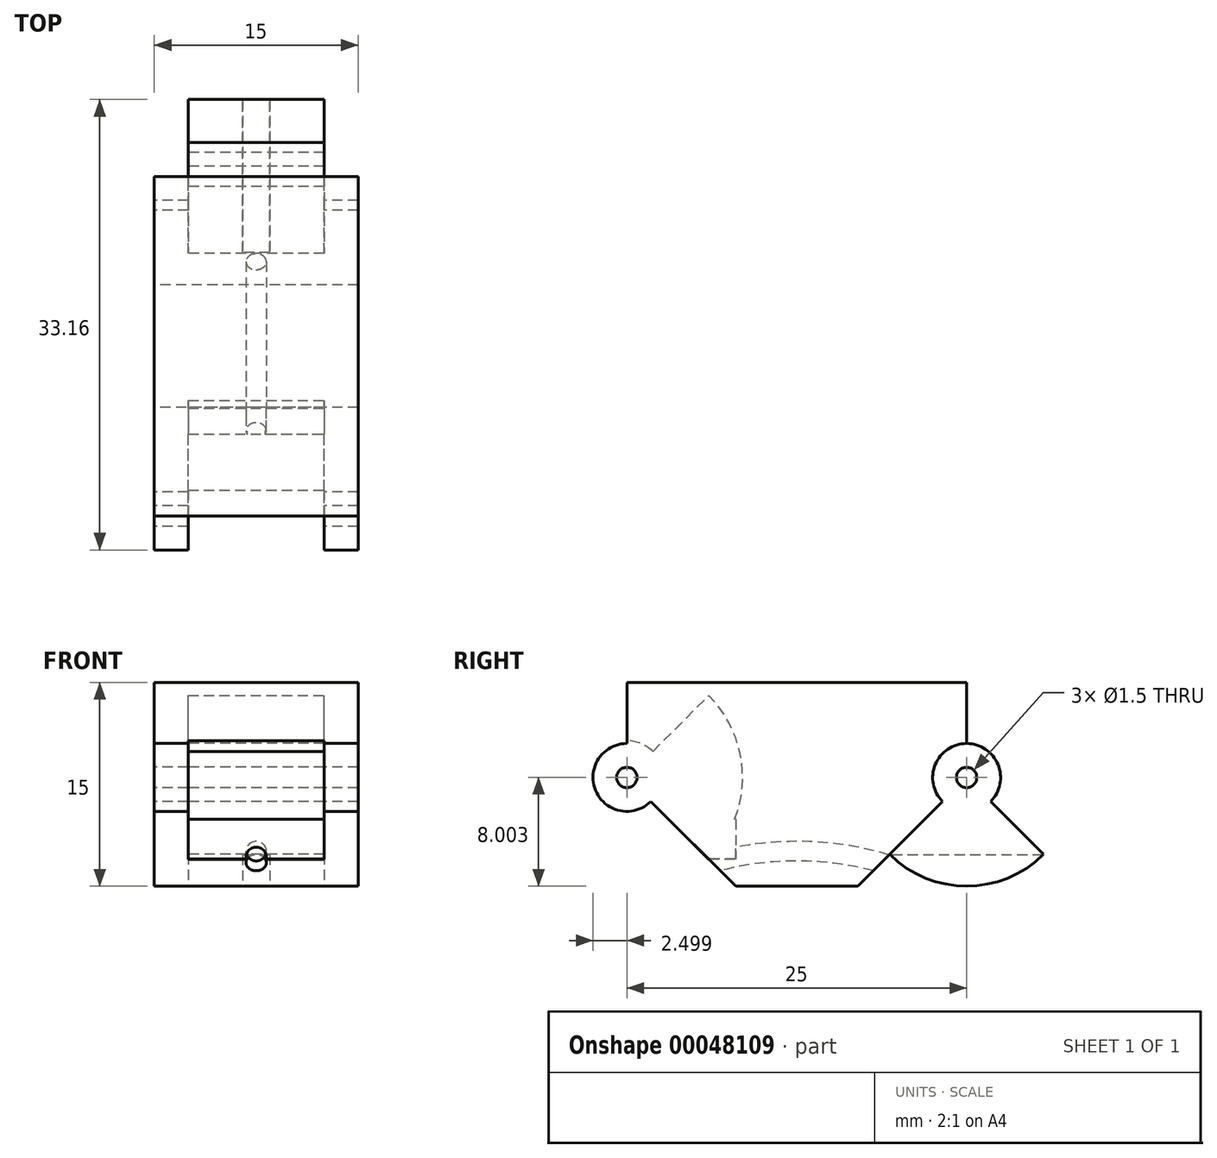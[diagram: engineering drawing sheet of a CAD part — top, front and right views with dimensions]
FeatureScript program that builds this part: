
annotation { "Feature Type Name" : "Feature", "Feature Type Description" : "" }
export const myFeature = defineFeature(function(context is Context, id is Id, definition is map)
    precondition{}
    {
        {
            var Q0;
            Q0=qCreatedBy(makeId("Right.planeOp"),FACE);
            var sketch = newSketch(context, id + "F0", { "sketchPlane" : qUnion([Q0])});
            skLineSegment(sketch, "E0.bottom", {"start": v(-39.16, 7.74) * mm, "end": v(-14.16, 7.74) * mm});
            skLineSegment(sketch, "E0.top", {"start": v(-39.16, -7.26) * mm, "end": v(-14.16, -7.26) * mm});
            skLineSegment(sketch, "E0.left", {"start": v(-39.16, 7.74) * mm, "end": v(-39.16, -7.26) * mm});
            skLineSegment(sketch, "E0.right", {"start": v(-14.16, 7.74) * mm, "end": v(-14.16, -7.26) * mm});
            skCircle(sketch, "E1", {"center": v(-14.16, 0.74) * mm, "radius": 2.5 * mm});
            skCircle(sketch, "E2", {"center": v(-14.16, 0.74) * mm, "radius": 8 * mm});
            skLineSegment(sketch, "E3", {"start": v(-14.16, 0.74) * mm, "end": v(-8.5, -4.91) * mm});
            skCircle(sketch, "E4", {"center": v(-14.16, 0.74) * mm, "radius": 0.75 * mm});
            skLineSegment(sketch, "E5", {"start": v(-14.16, 0.74) * mm, "end": v(-22.16, -7.26) * mm});
            skCircle(sketch, "E6", {"center": v(-39.16, 0.74) * mm, "radius": 2.5 * mm});
            skCircle(sketch, "E7", {"center": v(-39.16, 0.74) * mm, "radius": 0.75 * mm});
            skLineSegment(sketch, "E8", {"start": v(-39.16, 0.74) * mm, "end": v(-31.16, -7.26) * mm});
            skArc(sketch, "E9", {"start": v(-33.14, -5.28) * mm, "mid": v(-30.65, 0.74) * mm, "end": v(-33.14, 6.76) * mm});
            skLineSegment(sketch, "E10", {"start": v(-39.16, 0.74) * mm, "end": v(-32.16, 7.74) * mm});
            skSolve(sketch);
        }
        {
            var Q0;
            {var subQ3=sQuery(id+"F0.wireOp",EDGE,"E0.right");var subQ7=sQuery(id+"F0.wireOp",EDGE,"E0.bottom");var subQ8=makeQuery(id+"F0.imprint","INTERSECT",VERTEX,{"derivedFrom":[subQ7,subQ3]});Q0=makeQuery(id+"F0.imprint","IMPRINT",FACE,{"disambiguationData":[TD([[makeQuery(id+"F0.imprint","IMPRINT",EDGE,{"disambiguationData":[TD([[subQ8,1.0]])],"derivedFrom":subQ7}),-1.0]])]});}
            var Q1;
            {var subQ5=sQuery(id+"F0.wireOp",EDGE,"E0.left");var subQ11=sQuery(id+"F0.wireOp",EDGE,"E0.bottom");var subQ13=makeQuery(id+"F0.imprint","INTERSECT",VERTEX,{"derivedFrom":[subQ11,subQ5]});Q1=makeQuery(id+"F0.imprint","IMPRINT",FACE,{"disambiguationData":[TD([[makeQuery(id+"F0.imprint","IMPRINT",EDGE,{"disambiguationData":[TD([[subQ13,-1.0]])],"derivedFrom":subQ11}),-1.0]])]});}
            var Q2;
            {var subQ3=sQuery(id+"F0.wireOp",EDGE,"E6");var subQ5=sQuery(id+"F0.wireOp",EDGE,"E0.left");var subQ6=makeQuery(id+"F0.imprint","INTERSECT",VERTEX,{"disambiguationData":[OD(1.0)],"derivedFrom":[subQ5,subQ3]});Q2=makeQuery(id+"F0.imprint","IMPRINT",FACE,{"disambiguationData":[TD([[makeQuery(id+"F0.imprint","IMPRINT",EDGE,{"disambiguationData":[TD([[subQ6,1.0]])],"derivedFrom":subQ5}),1.0]])]});}
            var Q3;
            {var subQ1=sQuery(id+"F0.wireOp",EDGE,"E0.left");var subQ4=sQuery(id+"F0.wireOp",EDGE,"E6");var subQ6=makeQuery(id+"F0.imprint","INTERSECT",VERTEX,{"disambiguationData":[OD(0.0)],"derivedFrom":[subQ1,subQ4]});Q3=makeQuery(id+"F0.imprint","IMPRINT",FACE,{"disambiguationData":[TD([[makeQuery(id+"F0.imprint","IMPRINT",EDGE,{"disambiguationData":[TD([[subQ6,-1.0]])],"derivedFrom":subQ1}),-1.0]])]});}
            var Q4;
            {var subQ3=sQuery(id+"F0.wireOp",EDGE,"E6");var subQ5=sQuery(id+"F0.wireOp",EDGE,"E0.left");var subQ7=makeQuery(id+"F0.imprint","INTERSECT",VERTEX,{"disambiguationData":[OD(0.0)],"derivedFrom":[subQ5,subQ3]});Q4=makeQuery(id+"F0.imprint","IMPRINT",FACE,{"disambiguationData":[TD([[makeQuery(id+"F0.imprint","IMPRINT",EDGE,{"disambiguationData":[TD([[subQ7,-1.0]])],"derivedFrom":subQ5}),1.0]])]});}
            var Q5;
            {var subQ0=sQuery(id+"F0.wireOp",EDGE,"E9");Q5=makeQuery(id+"F0.imprint","IMPRINT",FACE,{"disambiguationData":[TD([[makeQuery(id+"F0.imprint","IMPRINT",EDGE,{"derivedFrom":subQ0}),-1.0]])]});}
            var Q6;
            {var subQ3=sQuery(id+"F0.wireOp",EDGE,"E9");Q6=makeQuery(id+"F0.imprint","IMPRINT",FACE,{"disambiguationData":[TD([[makeQuery(id+"F0.imprint","IMPRINT",EDGE,{"derivedFrom":subQ3}),1.0]])]});}
            var Q7;
            {var subQ0=sQuery(id+"F0.wireOp",EDGE,"E10");var subQ3=sQuery(id+"F0.wireOp",EDGE,"E6");var subQ4=makeQuery(id+"F0.imprint","INTERSECT",VERTEX,{"derivedFrom":[subQ3,subQ0]});Q7=makeQuery(id+"F0.imprint","IMPRINT",FACE,{"disambiguationData":[TD([[makeQuery(id+"F0.imprint","IMPRINT",EDGE,{"disambiguationData":[TD([[subQ4,1.0]])],"derivedFrom":subQ3}),1.0]])]});}
            extrude(context, id + "F1", {"entities" : qUnion([Q0, Q1, Q2, Q3, Q4, Q5, Q6, Q7]), "depth" : 15 * mm, "symmetric" : true});
        }
        {
            var Q0;
            {var subQ3=sQuery(id+"F0.wireOp",EDGE,"E1");var subQ5=sQuery(id+"F0.wireOp",EDGE,"E0.right");var subQ6=makeQuery(id+"F0.imprint","INTERSECT",VERTEX,{"disambiguationData":[OD(0.0)],"derivedFrom":[subQ5,subQ3]});Q0=makeQuery(id+"F0.imprint","IMPRINT",FACE,{"disambiguationData":[TD([[makeQuery(id+"F0.imprint","IMPRINT",EDGE,{"disambiguationData":[TD([[subQ6,-1.0]])],"derivedFrom":subQ5}),-1.0]])]});}
            var Q1;
            {var subQ3=sQuery(id+"F0.wireOp",EDGE,"E0.right");var subQ5=sQuery(id+"F0.wireOp",EDGE,"E1");var subQ7=makeQuery(id+"F0.imprint","INTERSECT",VERTEX,{"disambiguationData":[OD(0.0)],"derivedFrom":[subQ3,subQ5]});Q1=makeQuery(id+"F0.imprint","IMPRINT",FACE,{"disambiguationData":[TD([[makeQuery(id+"F0.imprint","IMPRINT",EDGE,{"disambiguationData":[TD([[subQ7,-1.0]])],"derivedFrom":subQ3}),1.0]])]});}
            var Q2;
            {var subQ1=sQuery(id+"F0.wireOp",EDGE,"E4");var subQ5=sQuery(id+"F0.wireOp",EDGE,"E0.right");var subQ7=makeQuery(id+"F0.imprint","INTERSECT",VERTEX,{"disambiguationData":[OD(1.0)],"derivedFrom":[subQ5,subQ1]});Q2=makeQuery(id+"F0.imprint","IMPRINT",FACE,{"disambiguationData":[TD([[makeQuery(id+"F0.imprint","IMPRINT",EDGE,{"disambiguationData":[TD([[subQ7,-1.0]])],"derivedFrom":subQ5}),1.0]])]});}
            var Q3;
            {var subQ0=sQuery(id+"F0.wireOp",EDGE,"E4");var subQ3=sQuery(id+"F0.wireOp",EDGE,"E0.right");var subQ4=makeQuery(id+"F0.imprint","INTERSECT",VERTEX,{"disambiguationData":[OD(1.0)],"derivedFrom":[subQ3,subQ0]});Q3=makeQuery(id+"F0.imprint","IMPRINT",FACE,{"disambiguationData":[TD([[makeQuery(id+"F0.imprint","IMPRINT",EDGE,{"disambiguationData":[TD([[subQ4,-1.0]])],"derivedFrom":subQ3}),-1.0]])]});}
            var Q4;
            {var subQ3=sQuery(id+"F0.wireOp",EDGE,"E0.right");var subQ5=sQuery(id+"F0.wireOp",EDGE,"E1");var subQ7=makeQuery(id+"F0.imprint","INTERSECT",VERTEX,{"disambiguationData":[OD(1.0)],"derivedFrom":[subQ3,subQ5]});Q4=makeQuery(id+"F0.imprint","IMPRINT",FACE,{"disambiguationData":[TD([[makeQuery(id+"F0.imprint","IMPRINT",EDGE,{"disambiguationData":[TD([[subQ7,1.0]])],"derivedFrom":subQ5}),-1.0]])]});}
            var Q5;
            {var subQ1=sQuery(id+"F0.wireOp",EDGE,"E1");var subQ5=sQuery(id+"F0.wireOp",EDGE,"E0.right");var subQ7=makeQuery(id+"F0.imprint","INTERSECT",VERTEX,{"disambiguationData":[OD(1.0)],"derivedFrom":[subQ5,subQ1]});Q5=makeQuery(id+"F0.imprint","IMPRINT",FACE,{"disambiguationData":[TD([[makeQuery(id+"F0.imprint","IMPRINT",EDGE,{"disambiguationData":[TD([[subQ7,-1.0]])],"derivedFrom":subQ1}),-1.0]])]});}
            extrude(context, id + "F2", {"entities" : qUnion([Q0, Q1, Q2, Q3, Q4, Q5]), "operationType" : NewBodyOperationType.ADD, "depth" : 10 * mm, "symmetric" : true});
        }
        {
            var Q0;
            Q0=qCreatedBy(makeId("Right.planeOp"),FACE);
            var sketch = newSketch(context, id + "F3", { "sketchPlane" : qUnion([Q0])});
            skCircle(sketch, "E11", {"center": v(-39.16, 0.74) * mm, "radius": 2.7 * mm});
            skSolve(sketch);
        }
        {
            var Q0;
            Q0=qSketchRegion(id+"F3",true);
            extrude(context, id + "F4", {"entities" : qUnion([Q0]), "operationType" : NewBodyOperationType.REMOVE, "oppositeDirection" : true, "depth" : 10 * mm, "symmetric" : true});
        }
        {
            var Q0;
            {var subQ0=sQuery(id+"F0.wireOp",EDGE,"E0.left");Q0=makeQuery(id+"F1.opExtrude","SWEPT_FACE",FACE,{"disambiguationData":[OSD([subQ0]),TDD([makeQuery(id+"F0.imprint","IMPRINT",EDGE,{"disambiguationData":[TD([[makeQuery(id+"F0.imprint","INTERSECT",VERTEX,{"derivedFrom":[sQuery(id+"F0.wireOp",EDGE,"E0.bottom"),subQ0]}),-1.0]])],"derivedFrom":subQ0})])]});}
            var sketch = newSketch(context, id + "F5", { "sketchPlane" : qUnion([Q0])});
            skLineSegment(sketch, "E12.bottom", {"start": v(5, -2.35) * mm, "end": v(-5, -2.35) * mm});
            skLineSegment(sketch, "E12.top", {"start": v(5, -5.26) * mm, "end": v(-5, -5.26) * mm});
            skLineSegment(sketch, "E12.left", {"start": v(5, -2.35) * mm, "end": v(5, -5.26) * mm});
            skLineSegment(sketch, "E12.right", {"start": v(-5, -2.35) * mm, "end": v(-5, -5.26) * mm});
            skSolve(sketch);
        }
        {
            var Q0;
            Q0=qSketchRegion(id+"F5",true);
            extrude(context, id + "F6", {"entities" : qUnion([Q0]), "operationType" : NewBodyOperationType.REMOVE, "oppositeDirection" : true, "depth" : 8 * mm});
        }
        {
            var Q0;
            {var subQ3=sQuery(id+"F0.wireOp",EDGE,"E9");Q0=makeQuery(id+"F0.imprint","IMPRINT",FACE,{"disambiguationData":[TD([[makeQuery(id+"F0.imprint","IMPRINT",EDGE,{"derivedFrom":subQ3}),1.0]])]});}
            extrude(context, id + "F7", {"entities" : qUnion([Q0]), "operationType" : NewBodyOperationType.REMOVE, "oppositeDirection" : true, "depth" : 10 * mm, "symmetric" : true});
        }
        {
            var Q0;
            Q0=makeQuery(id+"F1.opExtrude","SWEPT_FACE",FACE,{"disambiguationData":[OSD([sQuery(id+"F0.wireOp",EDGE,"E0.top")])]});
            var sketch = newSketch(context, id + "F8", { "sketchPlane" : qUnion([Q0])});
            skLineSegment(sketch, "E13.rect.bottom", {"start": v(-1, 8.47) * mm, "end": v(1, 8.47) * mm});
            skLineSegment(sketch, "E13.rect.top", {"start": v(-1, 19.85) * mm, "end": v(1, 19.85) * mm});
            skLineSegment(sketch, "E13.rect.left", {"start": v(-1, 8.47) * mm, "end": v(-1, 19.85) * mm});
            skLineSegment(sketch, "E13.rect.right", {"start": v(1, 8.47) * mm, "end": v(1, 19.85) * mm});
            skPoint(sketch, "E13.rect.middle", {"position": v(0, 14.16) * mm});
            skSolve(sketch);
        }
        {
            var Q0;
            Q0=qSketchRegion(id+"F8",true);
            extrude(context, id + "F9", {"entities" : qUnion([Q0]), "operationType" : NewBodyOperationType.REMOVE, "oppositeDirection" : true, "depth" : 2.3 * mm});
        }
        {
            var Q0;
            Q0=makeQuery(id+"F1.opExtrude","SWEPT_FACE",FACE,{"disambiguationData":[OSD([sQuery(id+"F0.wireOp",EDGE,"E0.left")])]});
            cPlane(context, id + "F10", {"entities" : qUnion([Q0]), "cplaneType" : CPlaneType.OFFSET, "offset" : 6.02 * mm, "oppositeDirection" : true, "width" : 150 * mm, "height" : 150 * mm});
        }
        {
            var Q0;
            Q0=qCreatedBy(id+"F10.planeOp",FACE);
            var sketch = newSketch(context, id + "F11", { "sketchPlane" : qUnion([Q0])});
            skCircle(sketch, "E14", {"center": v(0, -5.61) * mm, "radius": 0.75 * mm});
            skSolve(sketch);
        }
        {
            var Q0;
            Q0=qCreatedBy(makeId("Right.planeOp"),FACE);
            var sketch = newSketch(context, id + "F12", { "sketchPlane" : qUnion([Q0])});
            skArc(sketch, "E15", {"start": v(-20.2, -5.61) * mm, "mid": v(-26.67, -4.68) * mm, "end": v(-33.14, -5.61) * mm});
            skSolve(sketch);
        }
        {
            var Q0;
            Q0=qSketchRegion(id+"F11",true);
            var Q1;
            Q1=qConstructionFilter(qBodyType(qCreatedBy(id+"F12",EDGE),BodyType.WIRE),ConstructionObject.NO);
            sweep(context, id + "F13", {"operationType" : NewBodyOperationType.REMOVE, "profiles" : qUnion([Q0]), "path" : qUnion([Q1])});
        }
    });
